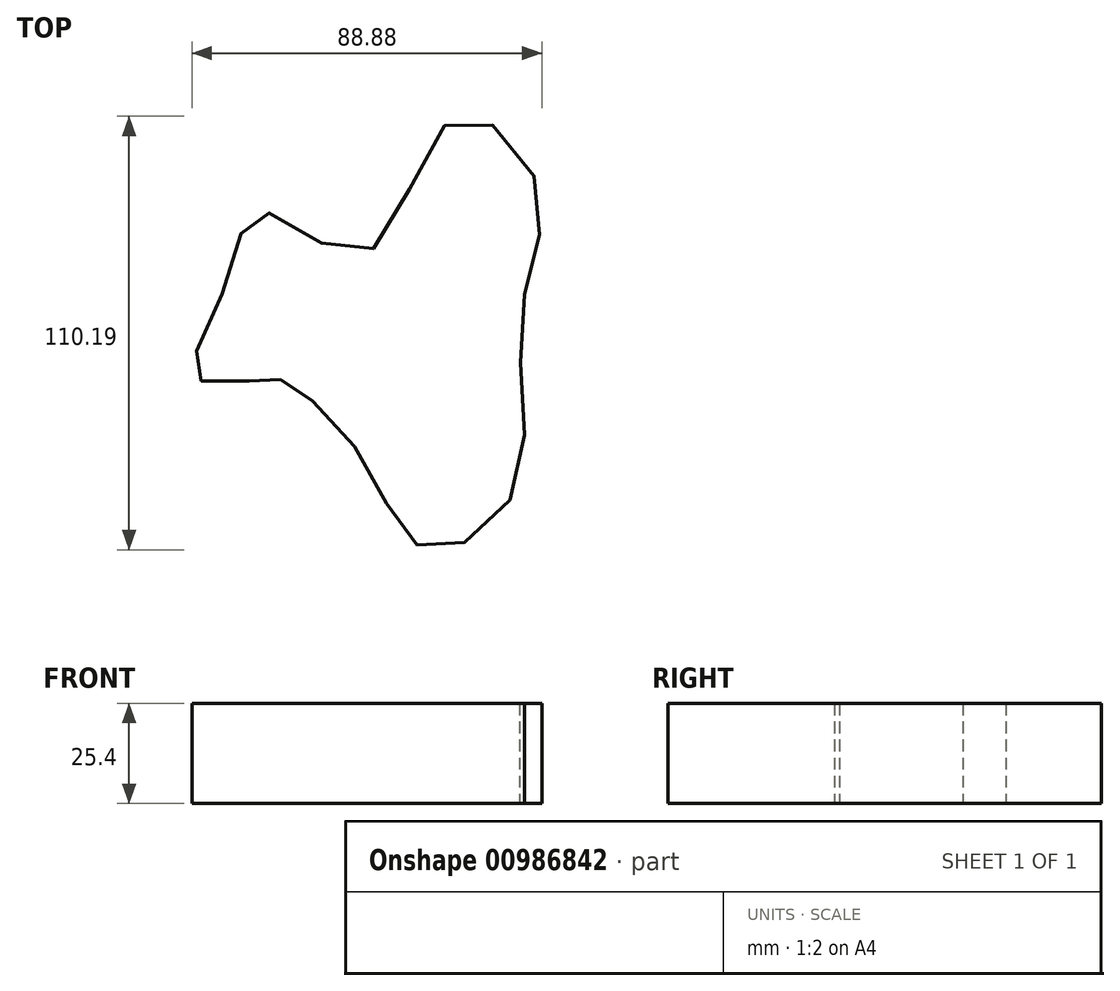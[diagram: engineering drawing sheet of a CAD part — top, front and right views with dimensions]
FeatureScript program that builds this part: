
annotation { "Feature Type Name" : "Feature", "Feature Type Description" : "" }
export const myFeature = defineFeature(function(context is Context, id is Id, definition is map)
    precondition{}
    {
        {
            var Q0;
            Q0=qCreatedBy(makeId("Top.planeOp"),FACE);
            var sketch = newSketch(context, id + "F0", { "sketchPlane" : qUnion([Q0])});
            skFitSpline(sketch, "E0", {"points": [v(-31.32, 5.99) * mm, v(-21.32, 26.93) * mm, v(4.9, 16.35) * mm, v(27.42, 50.46) * mm, v(48.93, 33.2) * mm, v(44.45, 0) * mm, v(42.83, -44.2) * mm, v(20.15, -58.6) * mm, v(4.18, -35.5) * mm, v(-15.14, -16.33) * mm, v(-20.81, -15.64) * mm, v(-38.24, -15.15) * mm, v(-31.32, 5.99) * mm]});
            skSolve(sketch);
        }
        {
            var Q0;
            Q0=makeQuery(id+"F0.imprint","IMPRINT",FACE,{"disambiguationData":[TD([[makeQuery(id+"F0.imprint","IMPRINT",EDGE,{"derivedFrom":sQuery(id+"F0.wireOp",EDGE,"E0")}),-1.0]])]});
            extrude(context, id + "F1", {"entities" : qUnion([Q0]), "depth" : 25.4 * mm, "offsetDistance" : 25.4 * mm});
        }
    });
